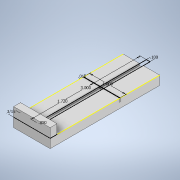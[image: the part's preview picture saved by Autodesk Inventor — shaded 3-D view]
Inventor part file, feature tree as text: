
AUTODESK INVENTOR PART (.ipt)
format: ipt  version: 2020 (Build 240168000, 168)  size: 134,144 bytes
history: native  units: in
note: dims shown in document units (in); Inventor stores cm internally (conversion verified against a paired STEP export)
features: extrude x4, sketch x2
ambient origin geometry x8: Origin, YZ Plane, XZ Plane, XY Plane, X Axis, Y Axis, Z Axis, Center Point
bodies: Solid1 (feature_tree)
feature tree (6):
  extrude  "Extrusion1"  Depth=3.0in
  sketch  "Sketch2"  dims[d2=0.25in d3=0.0in d4=0.1875in d5=0.05in d6=0.1in d7=3.0in d8=1.72in d9=1.0in d10=0.01in d11=0.25in d12=0.0in d13=0.05in d14=0.0in d15=0.1in d16=0.0in]
  extrude  "Extrusion2"  Depth=0.1875in
  extrude  "Extrusion3"  Depth=0.05in
  extrude  "Extrusion4"  Depth=0.1in
  sketch  "Sketch1"  dims[d0=1.0in d1=3.0in]
